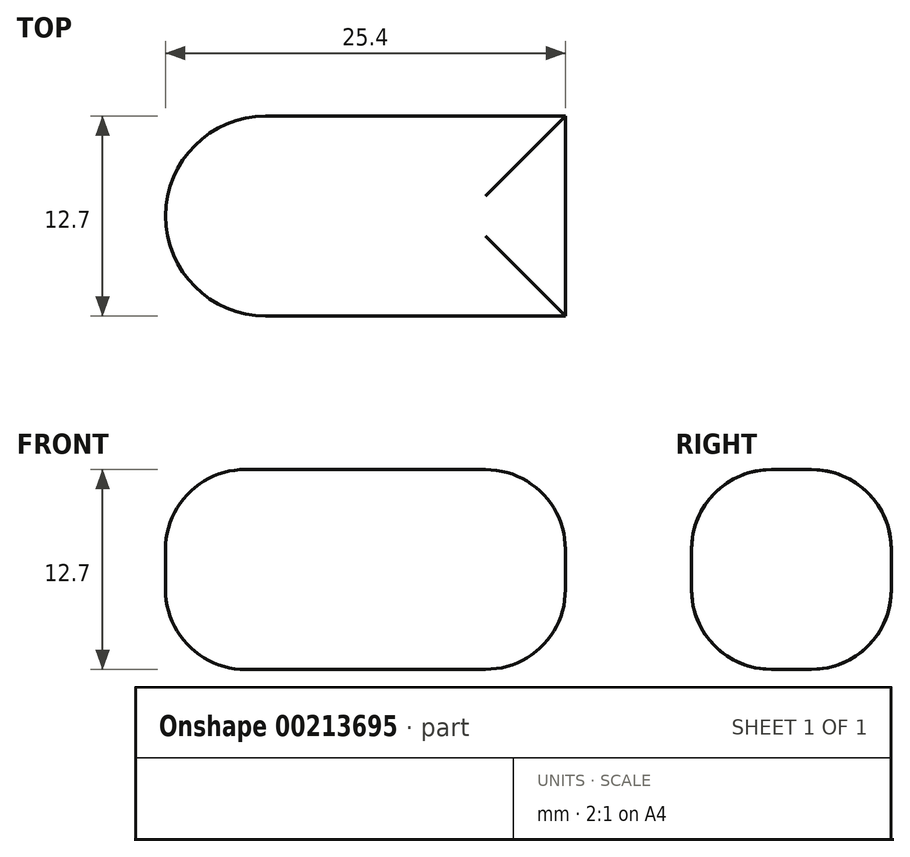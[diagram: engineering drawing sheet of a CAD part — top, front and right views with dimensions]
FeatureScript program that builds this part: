
annotation { "Feature Type Name" : "Feature", "Feature Type Description" : "" }
export const myFeature = defineFeature(function(context is Context, id is Id, definition is map)
    precondition{}
    {
        {
            var Q0;
            Q0=qCreatedBy(makeId("Top.planeOp"),FACE);
            var sketch = newSketch(context, id + "F0", { "sketchPlane" : qUnion([Q0])});
            skLineSegment(sketch, "E0.bottom", {"start": v(-19.05, 12.7) * mm, "end": v(0, 12.7) * mm});
            skLineSegment(sketch, "E0.top", {"start": v(-19.05, 0) * mm, "end": v(0, 0) * mm});
            skLineSegment(sketch, "E0.left", {"start": v(-25.4, 6.35) * mm, "end": v(-25.4, 6.35) * mm});
            skLineSegment(sketch, "E0.right", {"start": v(0, 12.7) * mm, "end": v(0, 0) * mm});
            skPoint(sketch, "E1.visualSharp", {"position": v(-25.4, 12.7) * mm});
            skArc(sketch, "E1.filletArc", {"start": v(-19.05, 12.7) * mm, "mid": v(-23.54, 10.84) * mm, "end": v(-25.4, 6.35) * mm});
            skPoint(sketch, "E2.visualSharp", {"position": v(-25.4, 0) * mm});
            skArc(sketch, "E2.filletArc", {"start": v(-25.4, 6.35) * mm, "mid": v(-23.54, 1.86) * mm, "end": v(-19.05, 0) * mm});
            skSolve(sketch);
        }
        {
            var Q0;
            Q0 = qSketchRegion(id + "F0", true);
            extrude(context, id + "F1", {"entities" : qUnion([Q0]), "depth" : 12.7 * mm});
        }
        {
            var Q0;
            Q0=makeQuery(id+"F1.opExtrude","CAP_FACE",FACE,{"disambiguationData":[OSD([sQuery(id+"F0.wireOp",EDGE,"E0.bottom"),sQuery(id+"F0.wireOp",EDGE,"E0.top"),sQuery(id+"F0.wireOp",EDGE,"E0.right"),sQuery(id+"F0.wireOp",EDGE,"E1.filletArc"),sQuery(id+"F0.wireOp",EDGE,"E2.filletArc")])],"isStart":false});
            var Q1;
            Q1=makeQuery(id+"F1.opExtrude","CAP_FACE",FACE,{"disambiguationData":[OSD([sQuery(id+"F0.wireOp",EDGE,"E0.bottom"),sQuery(id+"F0.wireOp",EDGE,"E0.top"),sQuery(id+"F0.wireOp",EDGE,"E0.right"),sQuery(id+"F0.wireOp",EDGE,"E1.filletArc"),sQuery(id+"F0.wireOp",EDGE,"E2.filletArc")])],"isStart":true});
            fillet(context, id + "F2", {"entities" : qUnion([Q0, Q1]), "radius" : 5.08 * mm, "tangentPropagation" : true, "allowEdgeOverflow" : false});
        }
    });
